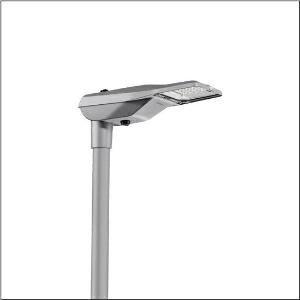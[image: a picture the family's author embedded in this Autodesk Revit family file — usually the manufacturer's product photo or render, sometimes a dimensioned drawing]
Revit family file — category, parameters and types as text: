
# Revit family: streetlight_sl_21_iq_micro___st1_0a_5xe1d61y08cb_da7e
name_source: partatom
category: Lighting Fixtures
units: mm (PartAtom-declared; Revit-internal decimal feet)

## family parameters
Cut with Voids When Loaded = No
Host = Face
Light Source = No
Part Type = Normal
Room Calculation Point = No
Round Connector Dimension = Use Diameter
Shared = No

## types (1)
- --- (1 x LED, 2500 lm, 19.1 W, 2700K)
    Apparent Load = 19 VA
    CIE Flux Codes = 37 72 97 100 100
    Color Rendering = 70
    Color Temperature = 2700K
    Default Elevation = 1800 mm
    Description = Streetlight SL 21 iQ micro, mast luminaire, primary light control with lens, of PMMA, primary optical cover: cover, of toughened safety glass, transparent, light distribution: ST1.0a, light emission: direct distribution, primary light characteristic: asymmetric, installation type: post-top, side-entry, LED, High Power LED, rated luminous flux: 2.500lm, luminous efficacy: 131lm/W, light colour: 727, colour temperature: 2700K, control: presetting dimming logarithmic, Street-Remote, Auto-Match, Temp-Guard, Lumen-Switch, Night-Set, Smart-Wire, Light-Fading, Desk-Remote (wireless, voltage-free reading and setting of iQ features in the workshop via application-optimized NFC function/RFID function), optimised constant luminous flux control (CLO 2.0), mains connection: 220..240V, AC, 50/60Hz, start of lifetime: 19W, end of service life: 20W, reduction: 9W, luminaire housing, of diecast aluminium, powder-coated, Siteco® metallic grey (DB 702S), corrosivity category C5 mid according to DIN EN ISO 12944, please order mast flange separately, inclination adjustable: 0°, 5°, 10°, 15°, sealing non-destructively replaceable, multi-level sealing system, length: 528mm, width: 235mm, height: 110mm, mast flange for spigot size: 42mm (side-entry): 5XC10008XM4, 60/48mm (side-entry/post-top): 5XC10108XM2, 76/60mm (side-entry/post-top): 5XC10108XM1, Smart Interface below and above, protection rating (complete): IP66, insulation class (complete): insulation class II (safety insulation), certification: CE, ENEC, ENEC+, VDE, impact resistance: IK09, permissible operating ambient temperature for outdoor applications: -40..+50°C, standard-compliant lighting for roads and squares, packaging unit: 1 piece

Light Distribution: ST1.0a
    Height = 110 mm
    Lamp = 1 x LED
    Lamp Light Flux = 2500 lm
    Lamp Power = 19.1 W
    Lamp count = 1
    Length = 528 mm
    Luminous efficacy = 131 lm/W
    Manufacturer = Siteco
    ModVariant = No
    Model = 5XE1D61Y08CB
    Number of Poles = 1
    OnlyDefault = Yes
    Power Factor = 1
    Product Name = Streetlight SL 21 iQ micro | ST1.0a
    Product group = mast luminaire | pylon top
    ProductGroupID = 6100
    Protection Class = Protection class II
    Protection Degree = IP 66
    RLX_Detail_Level = 1
    RLX_Emergency_Light_Flux = 0 lm
    RLX_Emergency_Type = 0
    RLX_Emergency_Type_DB = No
    RlxData = <blob elided: 98381 chars, md5=223a0575>
    Socket = socket
    Standby Power = 0 W
    System Light Flux = 2500 lm
    System Power = 19 W
    Type Comments = factory setting: luminous flux: 100 % | dim-lin: 254 | 387 mA
    Type Image = l_1007239.jpg
    URL = http://relux.com
    VarID = @adj_045571
    Voltage = 0 V
    Weight = 0.00 kg
    Width = 235 mm

## geometry (parser evidence)
native form markers: Blend x4, Sweep x12
no freeform markers — native parametric forms only
